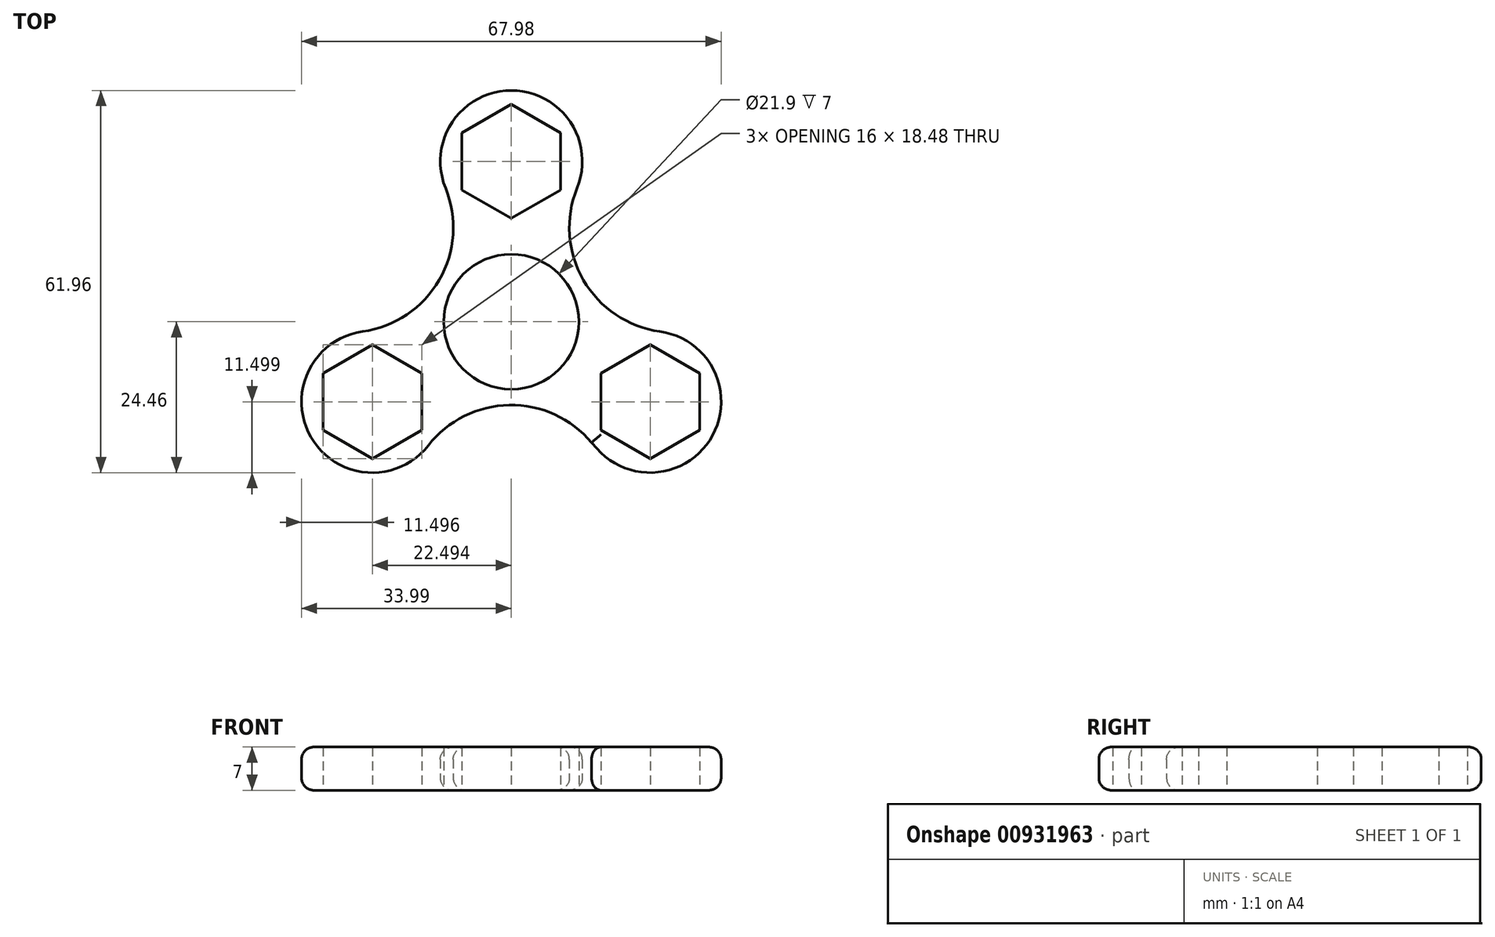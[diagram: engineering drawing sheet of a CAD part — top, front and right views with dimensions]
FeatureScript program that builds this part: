
annotation { "Feature Type Name" : "Feature", "Feature Type Description" : "" }
export const myFeature = defineFeature(function(context is Context, id is Id, definition is map)
    precondition{}
    {
        {
            var Q0;
            Q0=qCreatedBy(makeId("Top.planeOp"),FACE);
            var sketch = newSketch(context, id + "F0", { "sketchPlane" : qUnion([Q0])});
            skCircle(sketch, "E0", {"center": v(0, 0) * mm, "radius": 10.95 * mm});
            skCircle(sketch, "E1.cCircle", {"center": v(0, 26) * mm, "radius": 8 * mm, "construction": true});
            skLineSegment(sketch, "E1.0", {"start": v(8, 30.62) * mm, "end": v(8, 21.38) * mm});
            skLineSegment(sketch, "E1.1", {"start": v(8, 21.38) * mm, "end": v(0, 16.76) * mm});
            skLineSegment(sketch, "E1.2", {"start": v(0, 16.76) * mm, "end": v(-8, 21.38) * mm});
            skLineSegment(sketch, "E1.3", {"start": v(-8, 21.38) * mm, "end": v(-8, 30.62) * mm});
            skLineSegment(sketch, "E1.4", {"start": v(-8, 30.62) * mm, "end": v(0, 35.24) * mm});
            skLineSegment(sketch, "E1.5", {"start": v(0, 35.24) * mm, "end": v(8, 30.62) * mm});
            skPoint(sketch, "E1.0.midPoint", {"position": v(8, 26) * mm});
            skLineSegment(sketch, "E2.1.0", {"start": v(-30.5, -17.58) * mm, "end": v(-30.5, -8.34) * mm});
            skLineSegment(sketch, "E2.1.1", {"start": v(-22.5, -3.72) * mm, "end": v(-14.5, -8.34) * mm});
            skLineSegment(sketch, "E2.1.2", {"start": v(-22.5, -22.2) * mm, "end": v(-30.5, -17.58) * mm});
            skLineSegment(sketch, "E2.1.3", {"start": v(-14.5, -8.34) * mm, "end": v(-14.5, -17.58) * mm});
            skPoint(sketch, "E2.1.4", {"position": v(-26.5, -6.03) * mm});
            skCircle(sketch, "E2.1.5", {"center": v(-22.5, -12.96) * mm, "radius": 8 * mm, "construction": true});
            skLineSegment(sketch, "E2.1.6", {"start": v(-14.5, -17.58) * mm, "end": v(-22.5, -22.2) * mm});
            skLineSegment(sketch, "E2.1.7", {"start": v(-30.5, -8.34) * mm, "end": v(-22.5, -3.72) * mm});
            skLineSegment(sketch, "E2.2.0", {"start": v(30.5, -17.58) * mm, "end": v(22.5, -22.2) * mm});
            skLineSegment(sketch, "E2.2.1", {"start": v(14.5, -17.58) * mm, "end": v(14.5, -8.34) * mm});
            skLineSegment(sketch, "E2.2.2", {"start": v(30.5, -8.34) * mm, "end": v(30.5, -17.58) * mm});
            skLineSegment(sketch, "E2.2.3", {"start": v(14.5, -8.34) * mm, "end": v(22.5, -3.72) * mm});
            skPoint(sketch, "E2.2.4", {"position": v(18.5, -19.89) * mm});
            skCircle(sketch, "E2.2.5", {"center": v(22.5, -12.96) * mm, "radius": 8 * mm, "construction": true});
            skLineSegment(sketch, "E2.2.6", {"start": v(22.5, -3.72) * mm, "end": v(30.5, -8.34) * mm});
            skLineSegment(sketch, "E2.2.7", {"start": v(22.5, -22.2) * mm, "end": v(14.5, -17.58) * mm});
            skPoint(sketch, "E2.center", {"position": v(0, 0.03) * mm});
            skArc(sketch, "E3", {"start": v(10.65, 21.67) * mm, "mid": v(0, 37.5) * mm, "end": v(-10.65, 21.67) * mm});
            skArc(sketch, "E4", {"start": v(-24.07, -1.57) * mm, "mid": v(-32.46, -18.7) * mm, "end": v(-13.43, -20.04) * mm});
            skArc(sketch, "E5", {"start": v(13.87, -20.57) * mm, "mid": v(32.63, -18.4) * mm, "end": v(24.07, -1.57) * mm});
            skArc(sketch, "E6", {"start": v(-24.07, -1.57) * mm, "mid": v(-11.68, 6.77) * mm, "end": v(-10.65, 21.67) * mm});
            skArc(sketch, "E7", {"start": v(10.65, 21.67) * mm, "mid": v(11.68, 6.77) * mm, "end": v(24.07, -1.57) * mm});
            skArc(sketch, "E8", {"start": v(13, -19.6) * mm, "mid": v(-0.32, -13.5) * mm, "end": v(-13.43, -20.04) * mm});
            skLineSegment(sketch, "E9", {"start": v(13, -19.6) * mm, "end": v(13.87, -20.57) * mm});
            skSolve(sketch);
        }
        {
            var Q0;
            Q0=makeQuery(id+"F0.imprint","IMPRINT",FACE,{"disambiguationData":[TD([[makeQuery(id+"F0.imprint","IMPRINT",EDGE,{"derivedFrom":sQuery(id+"F0.wireOp",EDGE,"E0")}),-1.0]])]});
            extrude(context, id + "F1", {"entities" : qUnion([Q0]), "depth" : 7 * mm, "offsetDistance" : 25 * mm});
        }
        {
            var Q0;
            Q0=makeQuery(id+"F1.opExtrude","CAP_EDGE",EDGE,{"disambiguationData":[OSD([sQuery(id+"F0.wireOp",EDGE,"E8")])],"isStart":false});
            var Q1;
            Q1=makeQuery(id+"F1.opExtrude","CAP_EDGE",EDGE,{"disambiguationData":[OSD([sQuery(id+"F0.wireOp",EDGE,"E8")])],"isStart":true});
            fillet(context, id + "F2", {"entities" : qUnion([Q0, Q1]), "radius" : 2 * mm, "tangentPropagation" : true, "allowEdgeOverflow" : false});
        }
    });
